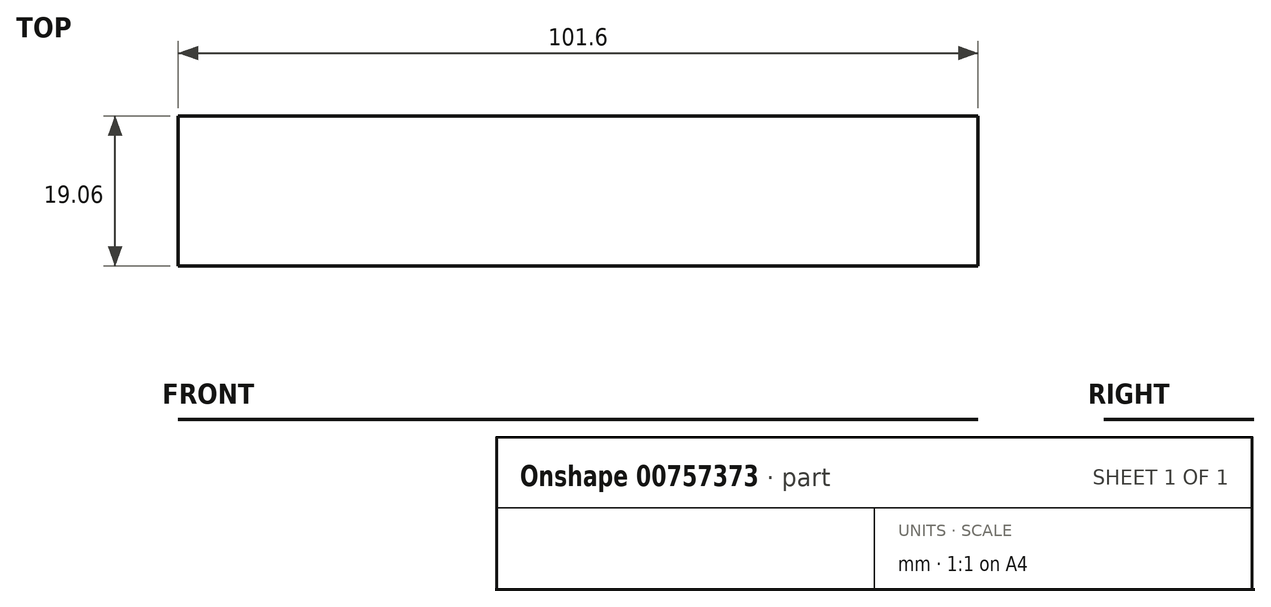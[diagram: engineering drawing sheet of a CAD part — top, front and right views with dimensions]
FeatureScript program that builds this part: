
annotation { "Feature Type Name" : "Feature", "Feature Type Description" : "" }
export const myFeature = defineFeature(function(context is Context, id is Id, definition is map)
    precondition{}
    {
        {
            var Q0;
            Q0=qCreatedBy(makeId("Top.planeOp"),FACE);
            var sketch = newSketch(context, id + "F0", { "sketchPlane" : qUnion([Q0])});
            skLineSegment(sketch, "E0.bottom", {"start": v(-50.8, -12.7) * mm, "end": v(50.8, -12.7) * mm});
            skLineSegment(sketch, "E0.top", {"start": v(-50.8, 12.7) * mm, "end": v(50.8, 12.7) * mm});
            skLineSegment(sketch, "E0.left", {"start": v(-50.8, -12.7) * mm, "end": v(-50.8, 12.7) * mm});
            skLineSegment(sketch, "E0.right", {"start": v(50.8, -12.7) * mm, "end": v(50.8, 12.7) * mm});
            skPoint(sketch, "E0.middle", {"position": v(0, 0) * mm});
            skSolve(sketch);
        }
        {
            var Q0;
            Q0=makeQuery(id+"F0.imprint","IMPRINT",FACE,{"disambiguationData":[TD([[makeQuery(id+"F0.imprint","IMPRINT",EDGE,{"derivedFrom":sQuery(id+"F0.wireOp",EDGE,"E0.bottom")}),1.0]])]});
            extrude(context, id + "F1", {"entities" : qUnion([Q0]), "depth" : 1 / 203.2 * mm, "offsetDistance" : 25.4 * mm});
        }
        {
            var Q0;
            Q0=makeQuery(id+"F1.opExtrude","CAP_EDGE",EDGE,{"disambiguationData":[OSD([sQuery(id+"F0.wireOp",EDGE,"E0.top")])],"isStart":false});
            chamfer(context, id + "F2", {"entities" : qUnion([Q0]), "width" : 3.17 * mm, "tangentPropagation" : true});
        }
        {
            var Q0;
            Q0=makeQuery(id+"F1.opExtrude","CAP_EDGE",EDGE,{"disambiguationData":[OSD([sQuery(id+"F0.wireOp",EDGE,"E0.bottom")])],"isStart":true});
            chamfer(context, id + "F3", {"entities" : qUnion([Q0]), "width" : 3.17 * mm, "tangentPropagation" : true});
        }
    });
